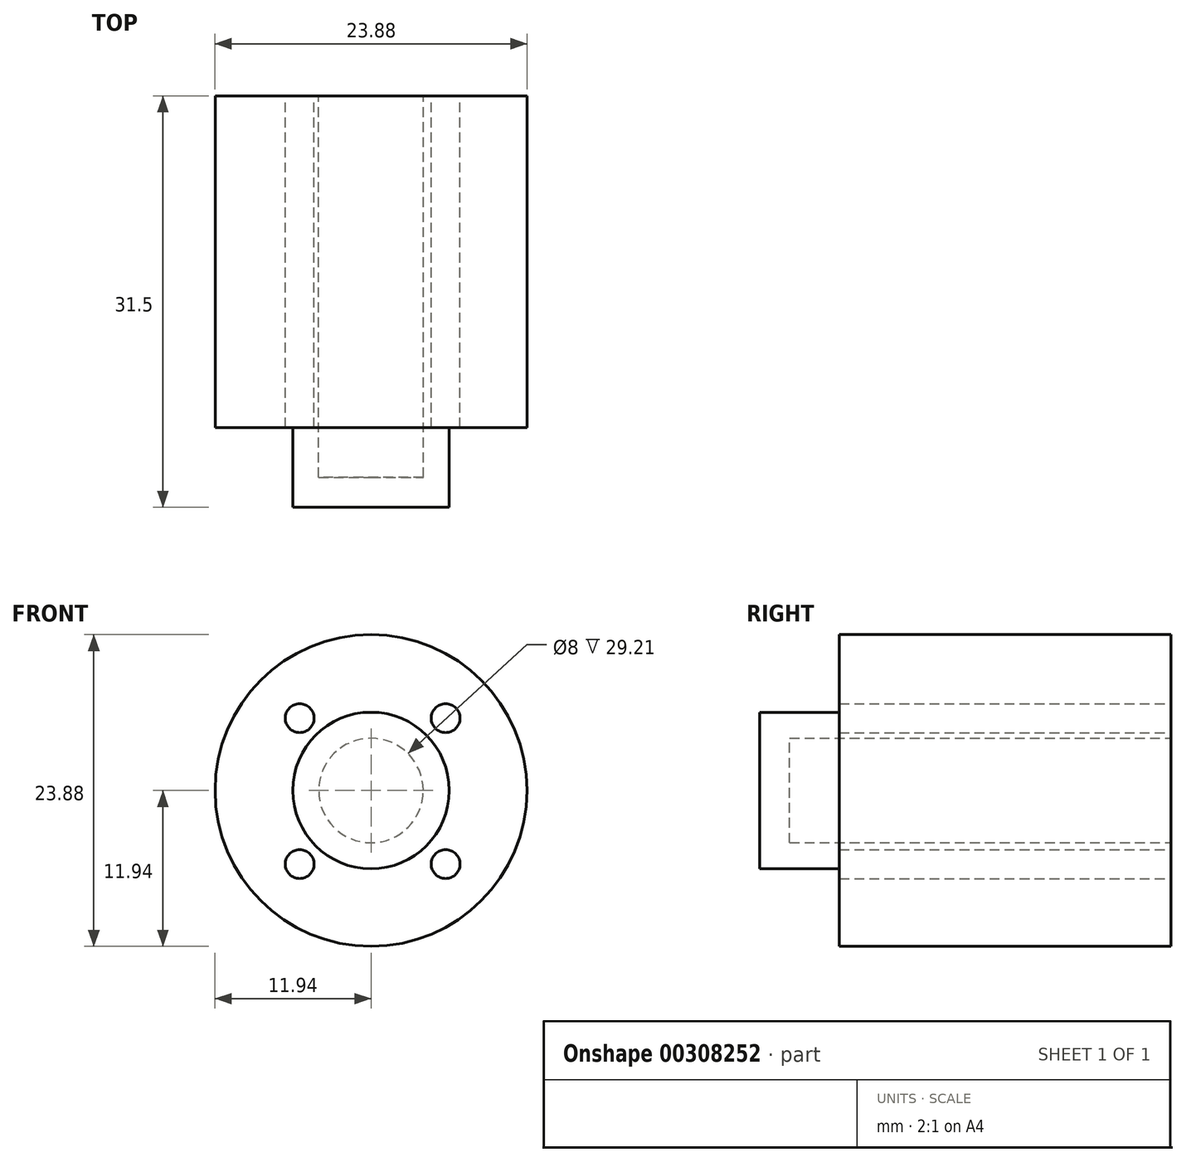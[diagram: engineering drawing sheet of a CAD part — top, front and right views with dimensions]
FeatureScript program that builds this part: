
annotation { "Feature Type Name" : "Feature", "Feature Type Description" : "" }
export const myFeature = defineFeature(function(context is Context, id is Id, definition is map)
    precondition{}
    {
        {
            var Q0;
            Q0=qCreatedBy(makeId("Front.planeOp"),FACE);
            var sketch = newSketch(context, id + "F0", { "sketchPlane" : qUnion([Q0])});
            skCircle(sketch, "E0", {"center": v(0, 0) * mm, "radius": 11.94 * mm});
            skCircle(sketch, "E1", {"center": v(0, 0) * mm, "radius": 6 * mm});
            skCircle(sketch, "E2", {"center": v(0, 0) * mm, "radius": 4 * mm});
            skCircle(sketch, "E3", {"center": v(-5.46, 5.54) * mm, "radius": 1.1 * mm});
            skCircle(sketch, "E4", {"center": v(-5.46, -5.64) * mm, "radius": 1.1 * mm});
            skCircle(sketch, "E5", {"center": v(5.71, -5.64) * mm, "radius": 1.1 * mm});
            skCircle(sketch, "E6", {"center": v(5.71, 5.54) * mm, "radius": 1.1 * mm});
            skPoint(sketch, "E7", {"position": v(-11.94, 0) * mm});
            skPoint(sketch, "E8", {"position": v(11.94, 0) * mm});
            skSolve(sketch);
        }
        {
            var Q0;
            Q0=makeQuery(id+"F0.imprint","IMPRINT",FACE,{"disambiguationData":[TD([[makeQuery(id+"F0.imprint","IMPRINT",EDGE,{"derivedFrom":sQuery(id+"F0.wireOp",EDGE,"E0")}),1.0]])]});
            extrude(context, id + "F1", {"entities" : qUnion([Q0]), "depth" : 25.4 * mm});
        }
        {
            var Q0;
            Q0=makeQuery(id+"F0.imprint","IMPRINT",FACE,{"disambiguationData":[TD([[makeQuery(id+"F0.imprint","IMPRINT",EDGE,{"derivedFrom":sQuery(id+"F0.wireOp",EDGE,"E1")}),1.0]])]});
            extrude(context, id + "F2", {"entities" : qUnion([Q0]), "operationType" : NewBodyOperationType.ADD, "depth" : 31.5 * mm});
        }
        {
            var Q0;
            Q0=makeQuery(id+"F0.imprint","IMPRINT",FACE,{"disambiguationData":[TD([[makeQuery(id+"F0.imprint","IMPRINT",EDGE,{"derivedFrom":sQuery(id+"F0.wireOp",EDGE,"E2")}),1.0]])]});
            extrude(context, id + "F3", {"entities" : qUnion([Q0]), "operationType" : NewBodyOperationType.ADD, "depth" : 31.5 * mm});
        }
        {
            var Q0;
            Q0=makeQuery(id+"F0.imprint","IMPRINT",FACE,{"disambiguationData":[TD([[makeQuery(id+"F0.imprint","IMPRINT",EDGE,{"derivedFrom":sQuery(id+"F0.wireOp",EDGE,"E2")}),1.0]])]});
            var sketch = newSketch(context, id + "F4", { "sketchPlane" : qUnion([Q0])});
            skCircle(sketch, "E9.0", {"center": v(0, 0) * mm, "radius": 4 * mm});
            skSolve(sketch);
        }
        {
            var Q0;
            Q0 = qSketchRegion(id + "F4", true);
            var Q1;
            Q1=makeQuery(id+"F0.imprint","IMPRINT",FACE,{"disambiguationData":[TD([[makeQuery(id+"F0.imprint","IMPRINT",EDGE,{"derivedFrom":sQuery(id+"F0.wireOp",EDGE,"E2")}),1.0]])]});
            extrude(context, id + "F5", {"entities" : qUnion([Q0, Q1]), "operationType" : NewBodyOperationType.REMOVE, "depth" : 29.2 * mm});
        }
    });
